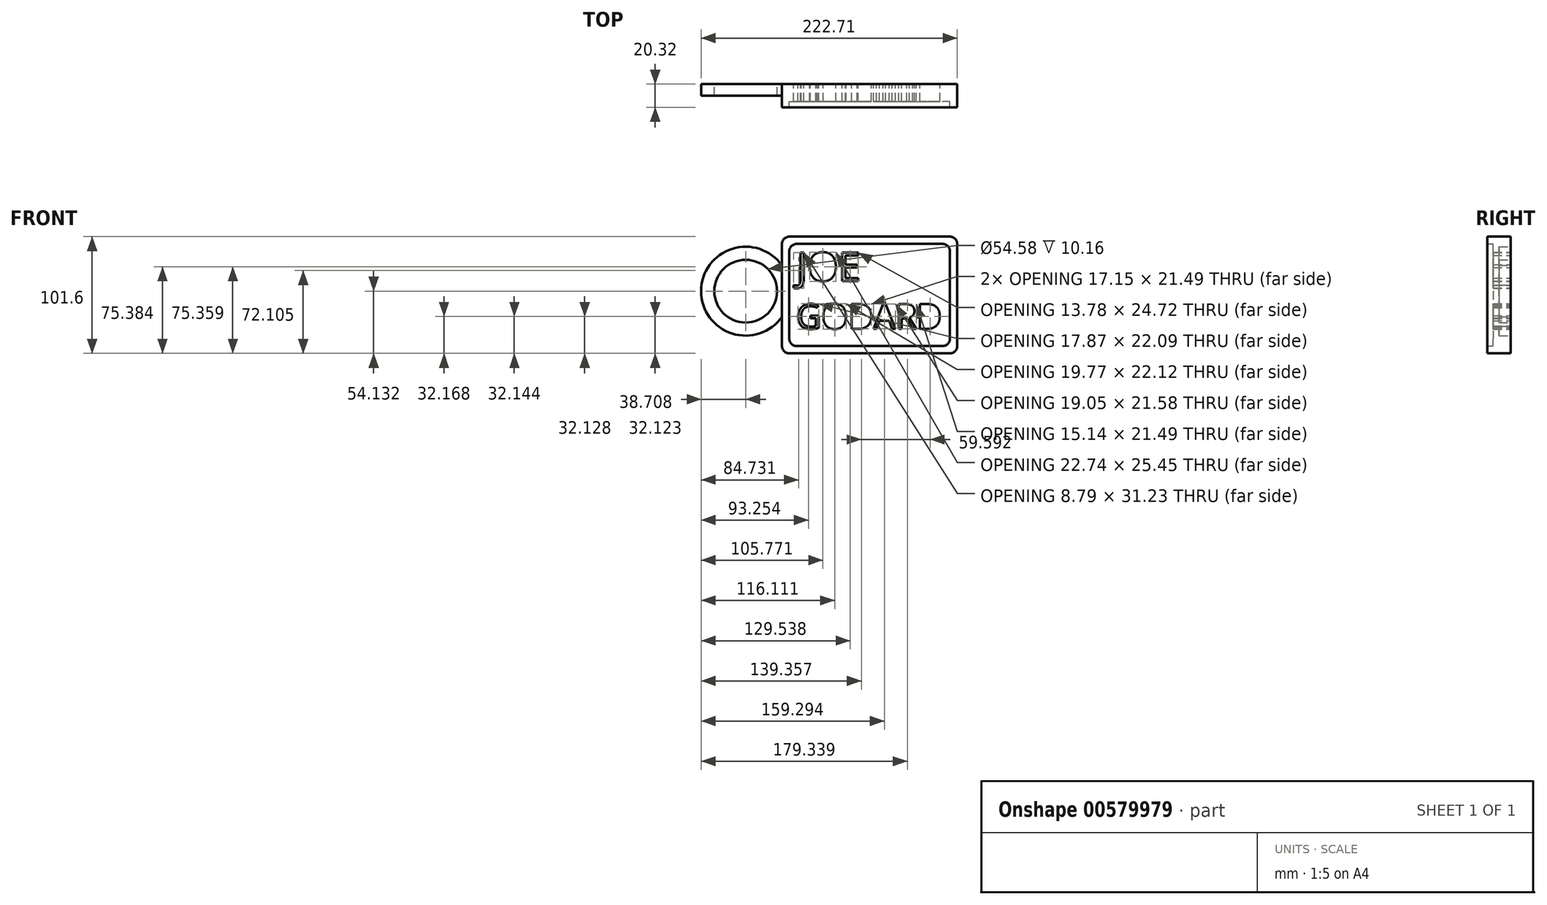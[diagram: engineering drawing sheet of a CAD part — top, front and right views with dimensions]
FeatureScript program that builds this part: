
annotation { "Feature Type Name" : "Feature", "Feature Type Description" : "" }
export const myFeature = defineFeature(function(context is Context, id is Id, definition is map)
    precondition{}
    {
        {
            var Q0;
            Q0=qCreatedBy(makeId("Front.planeOp"),FACE);
            var sketch = newSketch(context, id + "F0", { "sketchPlane" : qUnion([Q0])});
            skLineSegment(sketch, "E0.bottom", {"start": v(6.35, 0) * mm, "end": v(146.05, 0) * mm});
            skLineSegment(sketch, "E0.top", {"start": v(6.35, 101.6) * mm, "end": v(146.05, 101.6) * mm});
            skLineSegment(sketch, "E0.left", {"start": v(0, 6.35) * mm, "end": v(0, 31.78) * mm});
            skLineSegment(sketch, "E0.right", {"start": v(152.4, 6.35) * mm, "end": v(152.4, 95.25) * mm});
            skText(sketch, "E1", { "text": "JOE", "fontName": "OpenSans-Regular.ttf"});
            skText(sketch, "E2", { "text": "GODARD", "fontName": "OpenSans-Regular.ttf"});
            skArc(sketch, "E3", {"start": v(0, 76.48) * mm, "mid": v(-70.3, 54.13) * mm, "end": v(0, 31.78) * mm});
            skCircle(sketch, "E4", {"center": v(-31.6, 54.13) * mm, "radius": 27.3 * mm});
            skLineSegment(sketch, "E5.trimOffspring", {"start": v(0, 76.48) * mm, "end": v(0, 95.25) * mm});
            skPoint(sketch, "E6.visualSharp", {"position": v(0, 101.6) * mm});
            skArc(sketch, "E6.filletArc", {"start": v(6.35, 101.6) * mm, "mid": v(1.86, 99.74) * mm, "end": v(0, 95.25) * mm});
            skPoint(sketch, "E7.visualSharp", {"position": v(152.4, 101.6) * mm});
            skArc(sketch, "E7.filletArc", {"start": v(152.4, 95.25) * mm, "mid": v(150.54, 99.74) * mm, "end": v(146.05, 101.6) * mm});
            skPoint(sketch, "E8.visualSharp", {"position": v(152.4, 0) * mm});
            skArc(sketch, "E8.filletArc", {"start": v(146.05, 0) * mm, "mid": v(150.54, 1.86) * mm, "end": v(152.4, 6.35) * mm});
            skPoint(sketch, "E9.visualSharp", {"position": v(0, 0) * mm});
            skArc(sketch, "E9.filletArc", {"start": v(0, 6.35) * mm, "mid": v(1.86, 1.86) * mm, "end": v(6.35, 0) * mm});
            skLineSegment(sketch, "E10.bottom", {"start": v(12.7, 95.25) * mm, "end": v(139.7, 95.25) * mm});
            skLineSegment(sketch, "E10.top", {"start": v(12.7, 6.35) * mm, "end": v(139.7, 6.35) * mm});
            skLineSegment(sketch, "E10.left", {"start": v(6.35, 88.9) * mm, "end": v(6.35, 12.7) * mm});
            skLineSegment(sketch, "E10.right", {"start": v(146.05, 88.9) * mm, "end": v(146.05, 12.7) * mm});
            skArc(sketch, "E11.filletArc", {"start": v(12.7, 95.25) * mm, "mid": v(8.2, 93.4) * mm, "end": v(6.35, 88.9) * mm});
            skArc(sketch, "E12.filletArc", {"start": v(146.05, 88.9) * mm, "mid": v(144.2, 93.4) * mm, "end": v(139.7, 95.25) * mm});
            skArc(sketch, "E13.filletArc", {"start": v(139.7, 6.35) * mm, "mid": v(144.2, 8.2) * mm, "end": v(146.05, 12.7) * mm});
            skArc(sketch, "E14.filletArc", {"start": v(6.35, 12.7) * mm, "mid": v(8.2, 8.2) * mm, "end": v(12.7, 6.35) * mm});
            skLineSegment(sketch, "E15", {"start": v(0, 76.48) * mm, "end": v(0, 31.78) * mm});
            const initialGuessF0  = {"E1": [0.01273, 0.063, 1, 0, 0.02493], "E2": [0.01217, 0.02138, 1, 0, 0.02167]};
            skSetInitialGuess(sketch, initialGuessF0);
            skSolve(sketch);
        }
        {
            var Q0;
            Q0=makeQuery(id+"F0.imprint","IMPRINT",FACE,{"disambiguationData":[TD([[makeQuery(id+"F0.imprint","IMPRINT",EDGE,{"derivedFrom":sQuery(id+"F0.wireOp",EDGE,"E0.bottom")}),1.0]])]});
            extrude(context, id + "F1", {"entities" : qUnion([Q0]), "depth" : 20.32 * mm, "offsetDistance" : 25.4 * mm});
        }
        {
            var Q0;
            Q0=makeQuery(id+"F0.imprint","IMPRINT",FACE,{"disambiguationData":[TD([[makeQuery(id+"F0.imprint","IMPRINT",EDGE,{"derivedFrom":sQuery(id+"F0.wireOp",EDGE,"E1.sketch_text.stroke-0")}),1.0]])]});
            extrude(context, id + "F2", {"entities" : qUnion([Q0]), "operationType" : NewBodyOperationType.ADD, "depth" : 15.24 * mm, "offsetDistance" : 25.4 * mm});
        }
        {
            var Q0;
            Q0=makeQuery(id+"F0.imprint","IMPRINT",FACE,{"disambiguationData":[TD([[makeQuery(id+"F0.imprint","IMPRINT",EDGE,{"derivedFrom":sQuery(id+"F0.wireOp",EDGE,"E3")}),1.0]])]});
            extrude(context, id + "F3", {"entities" : qUnion([Q0]), "operationType" : NewBodyOperationType.ADD, "depth" : 10.16 * mm, "offsetDistance" : 25.4 * mm});
        }
    });
